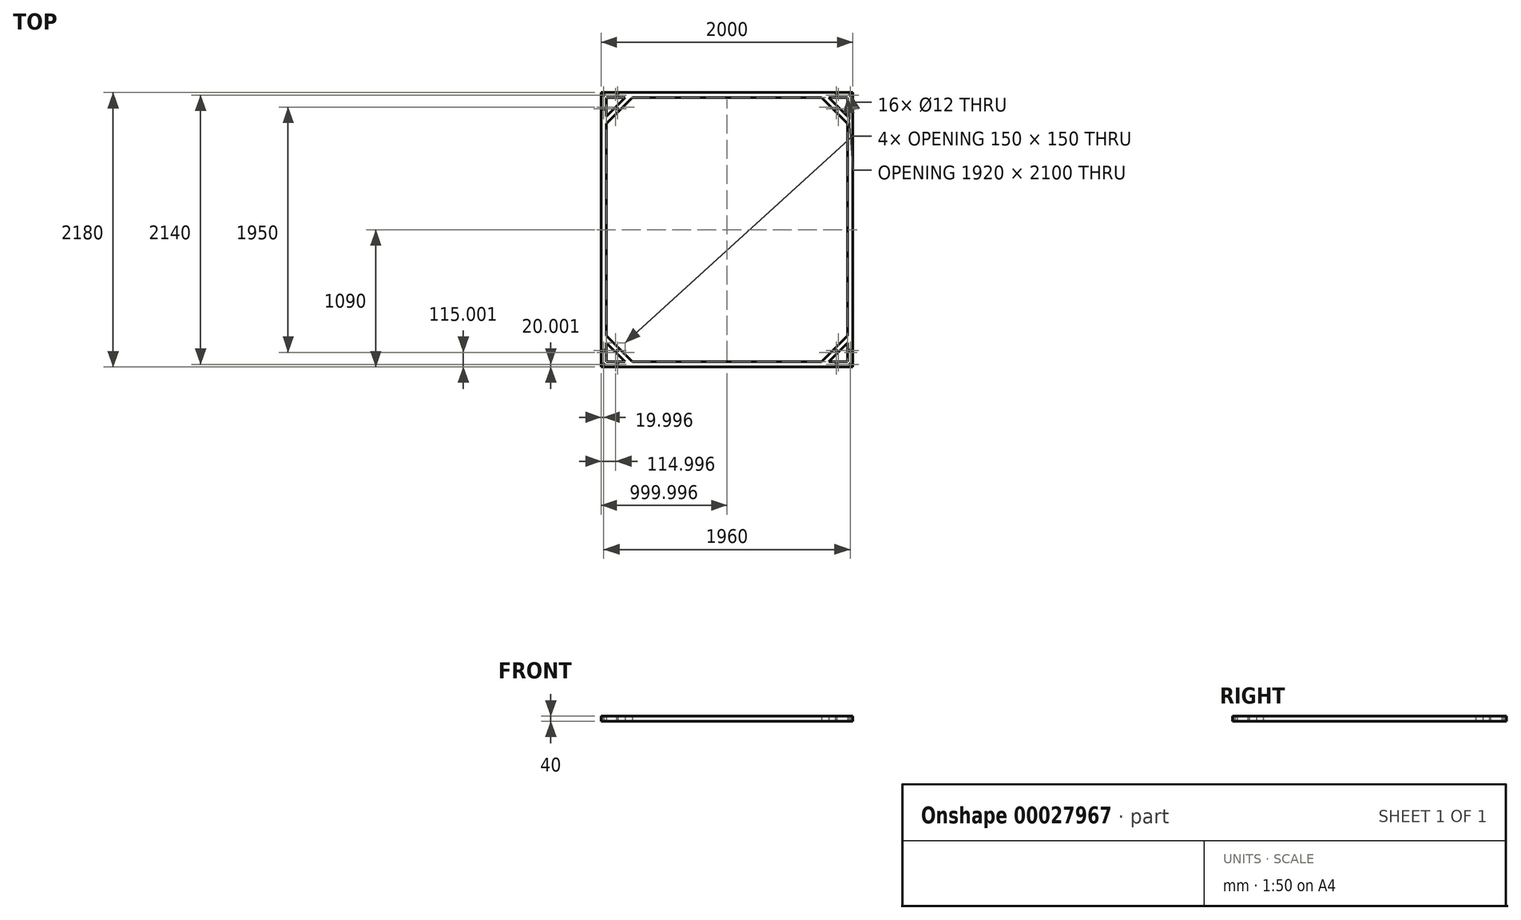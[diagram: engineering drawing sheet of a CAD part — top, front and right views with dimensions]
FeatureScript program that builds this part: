
annotation { "Feature Type Name" : "Feature", "Feature Type Description" : "" }
export const myFeature = defineFeature(function(context is Context, id is Id, definition is map)
    precondition{}
    {
        {
            var Q0;
            Q0=qCreatedBy(makeId("Top.planeOp"),FACE);
            var sketch = newSketch(context, id + "F0", { "sketchPlane" : qUnion([Q0])});
            skLineSegment(sketch, "E0.bottom", {"start": v(-446.06, 1599.63) * mm, "end": v(-406.06, 1599.63) * mm});
            skLineSegment(sketch, "E0.top", {"start": v(-446.06, -580.37) * mm, "end": v(-406.06, -580.37) * mm});
            skLineSegment(sketch, "E0.left", {"start": v(-446.06, 1599.63) * mm, "end": v(-446.06, -580.37) * mm});
            skLineSegment(sketch, "E0.right", {"start": v(-406.06, 1599.63) * mm, "end": v(-406.06, -580.37) * mm});
            skLineSegment(sketch, "E1.bottom", {"start": v(-406.06, 1599.63) * mm, "end": v(1513.94, 1599.63) * mm});
            skLineSegment(sketch, "E1.top", {"start": v(-406.06, 1559.63) * mm, "end": v(1513.94, 1559.63) * mm});
            skLineSegment(sketch, "E1.left", {"start": v(-406.06, 1599.63) * mm, "end": v(-406.06, 1559.63) * mm});
            skLineSegment(sketch, "E1.right", {"start": v(1513.94, 1599.63) * mm, "end": v(1513.94, 1559.63) * mm});
            skLineSegment(sketch, "E2.bottom", {"start": v(-406.06, -580.37) * mm, "end": v(1513.94, -580.37) * mm});
            skLineSegment(sketch, "E2.top", {"start": v(-406.06, -540.37) * mm, "end": v(1513.94, -540.37) * mm});
            skLineSegment(sketch, "E2.left", {"start": v(-406.06, -580.37) * mm, "end": v(-406.06, -540.37) * mm});
            skLineSegment(sketch, "E2.right", {"start": v(1513.94, -580.37) * mm, "end": v(1513.94, -540.37) * mm});
            skLineSegment(sketch, "E3", {"start": v(-406.06, 1409.63) * mm, "end": v(-256.06, 1559.63) * mm});
            skLineSegment(sketch, "E4", {"start": v(-256.06, 1559.63) * mm, "end": v(-199.5, 1559.63) * mm});
            skLineSegment(sketch, "E5", {"start": v(-199.5, 1559.63) * mm, "end": v(-406.06, 1353.06) * mm});
            skLineSegment(sketch, "E6", {"start": v(-406.06, 1353.06) * mm, "end": v(-406.06, 1409.63) * mm});
            skLineSegment(sketch, "E7.bottom", {"start": v(1513.94, 1599.63) * mm, "end": v(1553.94, 1599.63) * mm});
            skLineSegment(sketch, "E7.top", {"start": v(1513.94, -580.37) * mm, "end": v(1553.94, -580.37) * mm});
            skLineSegment(sketch, "E7.left", {"start": v(1513.94, 1599.63) * mm, "end": v(1513.94, -580.37) * mm});
            skLineSegment(sketch, "E7.right", {"start": v(1553.94, 1599.63) * mm, "end": v(1553.94, -580.37) * mm});
            skLineSegment(sketch, "E8", {"start": v(1513.94, 1409.63) * mm, "end": v(1363.94, 1559.63) * mm});
            skLineSegment(sketch, "E9", {"start": v(1363.94, 1559.63) * mm, "end": v(1307.37, 1559.63) * mm});
            skLineSegment(sketch, "E10", {"start": v(1307.37, 1559.63) * mm, "end": v(1513.94, 1353.06) * mm});
            skLineSegment(sketch, "E11", {"start": v(1513.94, 1353.06) * mm, "end": v(1513.94, 1409.63) * mm});
            skLineSegment(sketch, "E12", {"start": v(-256.06, -540.37) * mm, "end": v(-406.06, -390.37) * mm});
            skLineSegment(sketch, "E13", {"start": v(-406.06, -390.37) * mm, "end": v(-406.06, -333.8) * mm});
            skLineSegment(sketch, "E14", {"start": v(-406.06, -333.8) * mm, "end": v(-199.5, -540.37) * mm});
            skLineSegment(sketch, "E15", {"start": v(-199.5, -540.37) * mm, "end": v(-256.06, -540.37) * mm});
            skLineSegment(sketch, "E16", {"start": v(1363.94, -540.37) * mm, "end": v(1513.94, -390.37) * mm});
            skLineSegment(sketch, "E17", {"start": v(1513.94, -390.37) * mm, "end": v(1513.94, -333.8) * mm});
            skLineSegment(sketch, "E18", {"start": v(1513.94, -333.8) * mm, "end": v(1307.37, -540.37) * mm});
            skLineSegment(sketch, "E19", {"start": v(1307.37, -540.37) * mm, "end": v(1363.94, -540.37) * mm});
            skLineSegment(sketch, "E20", {"start": v(1307.37, 1559.63) * mm, "end": v(1363.94, 1559.63) * mm});
            skLineSegment(sketch, "E21", {"start": v(1513.94, 1409.63) * mm, "end": v(1513.94, 1353.06) * mm});
            skSolve(sketch);
        }
        {
            var Q0;
            Q0 = qSketchRegion(id + "F0", true);
            extrude(context, id + "F1", {"entities" : qUnion([Q0]), "depth" : 40 * mm});
        }
        {
            var Q0;
            Q0=makeQuery(id+"F0.imprint","IMPRINT",FACE,{"disambiguationData":[TD([[makeQuery(id+"F0.imprint","IMPRINT",EDGE,{"derivedFrom":sQuery(id+"F0.wireOp",EDGE,"E3")}),-1.0]])]});
            extrude(context, id + "F2", {"entities" : qUnion([Q0]), "operationType" : NewBodyOperationType.ADD, "depth" : 40 * mm});
        }
        {
            var Q0;
            Q0=makeQuery(id+"F0.imprint","IMPRINT",FACE,{"disambiguationData":[TD([[makeQuery(id+"F0.imprint","IMPRINT",EDGE,{"derivedFrom":sQuery(id+"F0.wireOp",EDGE,"E8")}),1.0]])]});
            extrude(context, id + "F3", {"entities" : qUnion([Q0]), "operationType" : NewBodyOperationType.ADD, "depth" : 40 * mm});
        }
        {
            var Q0;
            Q0=makeQuery(id+"F0.imprint","IMPRINT",FACE,{"disambiguationData":[TD([[makeQuery(id+"F0.imprint","IMPRINT",EDGE,{"derivedFrom":sQuery(id+"F0.wireOp",EDGE,"E12")}),-1.0]])]});
            extrude(context, id + "F4", {"entities" : qUnion([Q0]), "operationType" : NewBodyOperationType.ADD, "depth" : 40 * mm});
        }
        {
            var Q0;
            Q0=makeQuery(id+"F0.imprint","IMPRINT",FACE,{"disambiguationData":[TD([[makeQuery(id+"F0.imprint","IMPRINT",EDGE,{"derivedFrom":sQuery(id+"F0.wireOp",EDGE,"E16")}),1.0]])]});
            extrude(context, id + "F5", {"entities" : qUnion([Q0]), "operationType" : NewBodyOperationType.ADD, "depth" : 40 * mm});
        }
        {
            var Q0;
            {var subQ0=sQuery(id+"F0.wireOp",EDGE,"E4");var subQ1=sQuery(id+"F0.wireOp",EDGE,"E6");var subQ2=sQuery(id+"F0.wireOp",EDGE,"E13");var subQ3=sQuery(id+"F0.wireOp",EDGE,"E15");var subQ4=sQuery(id+"F0.wireOp",EDGE,"E17");var subQ5=sQuery(id+"F0.wireOp",EDGE,"E19");var subQ6=sQuery(id+"F0.wireOp",EDGE,"E20");var subQ7=sQuery(id+"F0.wireOp",EDGE,"E21");Q0=makeQuery(id+"F5.boolean.opBoolean","MERGE",FACE,{"derivedFrom":[makeQuery(id+"F4.boolean.opBoolean","MERGE",FACE,{"derivedFrom":[makeQuery(id+"F3.boolean.opBoolean","MERGE",FACE,{"derivedFrom":[makeQuery(id+"F2.boolean.opBoolean","MERGE",FACE,{"derivedFrom":[makeQuery(id+"F1.opExtrude","CAP_FACE",FACE,{"disambiguationData":[OSD([sQuery(id+"F0.wireOp",EDGE,"E0.bottom"),sQuery(id+"F0.wireOp",EDGE,"E0.top"),sQuery(id+"F0.wireOp",EDGE,"E0.left"),sQuery(id+"F0.wireOp",EDGE,"E0.right"),sQuery(id+"F0.wireOp",EDGE,"E1.bottom"),sQuery(id+"F0.wireOp",EDGE,"E1.top"),sQuery(id+"F0.wireOp",EDGE,"E2.bottom"),sQuery(id+"F0.wireOp",EDGE,"E2.top"),subQ0,subQ1,sQuery(id+"F0.wireOp",EDGE,"E7.bottom"),sQuery(id+"F0.wireOp",EDGE,"E7.top"),sQuery(id+"F0.wireOp",EDGE,"E7.left"),sQuery(id+"F0.wireOp",EDGE,"E7.right"),subQ2,subQ3,subQ4,subQ5,subQ6,subQ7])],"isStart":false}),makeQuery(id+"F2.opExtrude","CAP_FACE",FACE,{"disambiguationData":[OSD([sQuery(id+"F0.wireOp",EDGE,"E3"),subQ0,sQuery(id+"F0.wireOp",EDGE,"E5"),subQ1])],"isStart":false})]}),makeQuery(id+"F3.opExtrude","CAP_FACE",FACE,{"disambiguationData":[OSD([sQuery(id+"F0.wireOp",EDGE,"E8"),sQuery(id+"F0.wireOp",EDGE,"E10"),subQ6,subQ7])],"isStart":false})]}),makeQuery(id+"F4.opExtrude","CAP_FACE",FACE,{"disambiguationData":[OSD([sQuery(id+"F0.wireOp",EDGE,"E12"),subQ2,sQuery(id+"F0.wireOp",EDGE,"E14"),subQ3])],"isStart":false})]}),makeQuery(id+"F5.opExtrude","CAP_FACE",FACE,{"disambiguationData":[OSD([sQuery(id+"F0.wireOp",EDGE,"E16"),subQ4,sQuery(id+"F0.wireOp",EDGE,"E18"),subQ5])],"isStart":false})]});}
            var sketch = newSketch(context, id + "F6", { "sketchPlane" : qUnion([Q0])});
            skCircle(sketch, "E22", {"center": v(-316.06, 1469.63) * mm, "radius": 6 * mm});
            skCircle(sketch, "E23", {"center": v(-426.06, 1469.63) * mm, "radius": 6 * mm});
            skCircle(sketch, "E24", {"center": v(-426.06, 1579.63) * mm, "radius": 6 * mm});
            skCircle(sketch, "E25", {"center": v(-316.06, 1579.63) * mm, "radius": 6 * mm});
            skSolve(sketch);
        }
        {
            var Q0;
            Q0=sQuery(id+"F6.wireOp",VERTEX,"E24.center");
            var Q1;
            Q1=sQuery(id+"F6.wireOp",VERTEX,"E25.center");
            var Q2;
            Q2=sQuery(id+"F6.wireOp",VERTEX,"E22.center");
            var Q3;
            Q3=sQuery(id+"F6.wireOp",VERTEX,"E23.center");
            var Q4;
            Q4=makeQuery(id+"F1.opExtrude","SWEPT_BODY",BODY,{"disambiguationData":[OSD([sQuery(id+"F0.wireOp",EDGE,"E0.bottom"),sQuery(id+"F0.wireOp",EDGE,"E0.top"),sQuery(id+"F0.wireOp",EDGE,"E0.left"),sQuery(id+"F0.wireOp",EDGE,"E0.right"),sQuery(id+"F0.wireOp",EDGE,"E1.bottom"),sQuery(id+"F0.wireOp",EDGE,"E1.top"),sQuery(id+"F0.wireOp",EDGE,"E2.bottom"),sQuery(id+"F0.wireOp",EDGE,"E2.top"),sQuery(id+"F0.wireOp",EDGE,"E4"),sQuery(id+"F0.wireOp",EDGE,"E6"),sQuery(id+"F0.wireOp",EDGE,"E7.bottom"),sQuery(id+"F0.wireOp",EDGE,"E7.top"),sQuery(id+"F0.wireOp",EDGE,"E7.left"),sQuery(id+"F0.wireOp",EDGE,"E7.right"),sQuery(id+"F0.wireOp",EDGE,"E13"),sQuery(id+"F0.wireOp",EDGE,"E15"),sQuery(id+"F0.wireOp",EDGE,"E17"),sQuery(id+"F0.wireOp",EDGE,"E19"),sQuery(id+"F0.wireOp",EDGE,"E20"),sQuery(id+"F0.wireOp",EDGE,"E21")])]});
            hole(context, id + "F7", {"style" : HoleStyle.SIMPLE, "holeDiameter" : 12 * mm, "endStyle" : HoleEndStyle.BLIND, "holeDepth" : 40 * mm, "locations" : qUnion([Q0, Q1, Q2, Q3]), "scope" : qUnion([Q4])});
        }
        {
            var Q0;
            {var subQ0=sQuery(id+"F0.wireOp",EDGE,"E4");var subQ1=sQuery(id+"F0.wireOp",EDGE,"E6");var subQ2=sQuery(id+"F0.wireOp",EDGE,"E13");var subQ3=sQuery(id+"F0.wireOp",EDGE,"E15");var subQ4=sQuery(id+"F0.wireOp",EDGE,"E17");var subQ5=sQuery(id+"F0.wireOp",EDGE,"E19");var subQ6=sQuery(id+"F0.wireOp",EDGE,"E20");var subQ7=sQuery(id+"F0.wireOp",EDGE,"E21");Q0=makeQuery(id+"F5.boolean.opBoolean","MERGE",FACE,{"derivedFrom":[makeQuery(id+"F4.boolean.opBoolean","MERGE",FACE,{"derivedFrom":[makeQuery(id+"F3.boolean.opBoolean","MERGE",FACE,{"derivedFrom":[makeQuery(id+"F2.boolean.opBoolean","MERGE",FACE,{"derivedFrom":[makeQuery(id+"F1.opExtrude","CAP_FACE",FACE,{"disambiguationData":[OSD([sQuery(id+"F0.wireOp",EDGE,"E0.bottom"),sQuery(id+"F0.wireOp",EDGE,"E0.top"),sQuery(id+"F0.wireOp",EDGE,"E0.left"),sQuery(id+"F0.wireOp",EDGE,"E0.right"),sQuery(id+"F0.wireOp",EDGE,"E1.bottom"),sQuery(id+"F0.wireOp",EDGE,"E1.top"),sQuery(id+"F0.wireOp",EDGE,"E2.bottom"),sQuery(id+"F0.wireOp",EDGE,"E2.top"),subQ0,subQ1,sQuery(id+"F0.wireOp",EDGE,"E7.bottom"),sQuery(id+"F0.wireOp",EDGE,"E7.top"),sQuery(id+"F0.wireOp",EDGE,"E7.left"),sQuery(id+"F0.wireOp",EDGE,"E7.right"),subQ2,subQ3,subQ4,subQ5,subQ6,subQ7])],"isStart":false}),makeQuery(id+"F2.opExtrude","CAP_FACE",FACE,{"disambiguationData":[OSD([sQuery(id+"F0.wireOp",EDGE,"E3"),subQ0,sQuery(id+"F0.wireOp",EDGE,"E5"),subQ1])],"isStart":false})]}),makeQuery(id+"F3.opExtrude","CAP_FACE",FACE,{"disambiguationData":[OSD([sQuery(id+"F0.wireOp",EDGE,"E8"),sQuery(id+"F0.wireOp",EDGE,"E10"),subQ6,subQ7])],"isStart":false})]}),makeQuery(id+"F4.opExtrude","CAP_FACE",FACE,{"disambiguationData":[OSD([sQuery(id+"F0.wireOp",EDGE,"E12"),subQ2,sQuery(id+"F0.wireOp",EDGE,"E14"),subQ3])],"isStart":false})]}),makeQuery(id+"F5.opExtrude","CAP_FACE",FACE,{"disambiguationData":[OSD([sQuery(id+"F0.wireOp",EDGE,"E16"),subQ4,sQuery(id+"F0.wireOp",EDGE,"E18"),subQ5])],"isStart":false})]});}
            var sketch = newSketch(context, id + "F8", { "sketchPlane" : qUnion([Q0])});
            skCircle(sketch, "E26", {"center": v(1423.94, 1579.63) * mm, "radius": 6 * mm});
            skCircle(sketch, "E27", {"center": v(1533.94, 1579.63) * mm, "radius": 6 * mm});
            skCircle(sketch, "E28", {"center": v(1423.94, 1469.63) * mm, "radius": 6 * mm});
            skCircle(sketch, "E29", {"center": v(1533.94, 1469.63) * mm, "radius": 6 * mm});
            skSolve(sketch);
        }
        {
            var Q0;
            Q0=sQuery(id+"F8.wireOp",VERTEX,"E26.center");
            var Q1;
            Q1=sQuery(id+"F8.wireOp",VERTEX,"E27.center");
            var Q2;
            Q2=sQuery(id+"F8.wireOp",VERTEX,"E28.center");
            var Q3;
            Q3=sQuery(id+"F8.wireOp",VERTEX,"E29.center");
            var Q4;
            Q4=makeQuery(id+"F1.opExtrude","SWEPT_BODY",BODY,{"disambiguationData":[OSD([sQuery(id+"F0.wireOp",EDGE,"E0.bottom"),sQuery(id+"F0.wireOp",EDGE,"E0.top"),sQuery(id+"F0.wireOp",EDGE,"E0.left"),sQuery(id+"F0.wireOp",EDGE,"E0.right"),sQuery(id+"F0.wireOp",EDGE,"E1.bottom"),sQuery(id+"F0.wireOp",EDGE,"E1.top"),sQuery(id+"F0.wireOp",EDGE,"E2.bottom"),sQuery(id+"F0.wireOp",EDGE,"E2.top"),sQuery(id+"F0.wireOp",EDGE,"E4"),sQuery(id+"F0.wireOp",EDGE,"E6"),sQuery(id+"F0.wireOp",EDGE,"E7.bottom"),sQuery(id+"F0.wireOp",EDGE,"E7.top"),sQuery(id+"F0.wireOp",EDGE,"E7.left"),sQuery(id+"F0.wireOp",EDGE,"E7.right"),sQuery(id+"F0.wireOp",EDGE,"E13"),sQuery(id+"F0.wireOp",EDGE,"E15"),sQuery(id+"F0.wireOp",EDGE,"E17"),sQuery(id+"F0.wireOp",EDGE,"E19"),sQuery(id+"F0.wireOp",EDGE,"E20"),sQuery(id+"F0.wireOp",EDGE,"E21")])]});
            hole(context, id + "F9", {"style" : HoleStyle.SIMPLE, "holeDiameter" : 12 * mm, "endStyle" : HoleEndStyle.THROUGH, "locations" : qUnion([Q0, Q1, Q2, Q3]), "scope" : qUnion([Q4])});
        }
        {
            var Q0;
            {var subQ0=sQuery(id+"F0.wireOp",EDGE,"E4");var subQ1=sQuery(id+"F0.wireOp",EDGE,"E6");var subQ2=sQuery(id+"F0.wireOp",EDGE,"E13");var subQ3=sQuery(id+"F0.wireOp",EDGE,"E15");var subQ4=sQuery(id+"F0.wireOp",EDGE,"E17");var subQ5=sQuery(id+"F0.wireOp",EDGE,"E19");var subQ6=sQuery(id+"F0.wireOp",EDGE,"E20");var subQ7=sQuery(id+"F0.wireOp",EDGE,"E21");Q0=makeQuery(id+"F5.boolean.opBoolean","MERGE",FACE,{"derivedFrom":[makeQuery(id+"F4.boolean.opBoolean","MERGE",FACE,{"derivedFrom":[makeQuery(id+"F3.boolean.opBoolean","MERGE",FACE,{"derivedFrom":[makeQuery(id+"F2.boolean.opBoolean","MERGE",FACE,{"derivedFrom":[makeQuery(id+"F1.opExtrude","CAP_FACE",FACE,{"disambiguationData":[OSD([sQuery(id+"F0.wireOp",EDGE,"E0.bottom"),sQuery(id+"F0.wireOp",EDGE,"E0.top"),sQuery(id+"F0.wireOp",EDGE,"E0.left"),sQuery(id+"F0.wireOp",EDGE,"E0.right"),sQuery(id+"F0.wireOp",EDGE,"E1.bottom"),sQuery(id+"F0.wireOp",EDGE,"E1.top"),sQuery(id+"F0.wireOp",EDGE,"E2.bottom"),sQuery(id+"F0.wireOp",EDGE,"E2.top"),subQ0,subQ1,sQuery(id+"F0.wireOp",EDGE,"E7.bottom"),sQuery(id+"F0.wireOp",EDGE,"E7.top"),sQuery(id+"F0.wireOp",EDGE,"E7.left"),sQuery(id+"F0.wireOp",EDGE,"E7.right"),subQ2,subQ3,subQ4,subQ5,subQ6,subQ7])],"isStart":false}),makeQuery(id+"F2.opExtrude","CAP_FACE",FACE,{"disambiguationData":[OSD([sQuery(id+"F0.wireOp",EDGE,"E3"),subQ0,sQuery(id+"F0.wireOp",EDGE,"E5"),subQ1])],"isStart":false})]}),makeQuery(id+"F3.opExtrude","CAP_FACE",FACE,{"disambiguationData":[OSD([sQuery(id+"F0.wireOp",EDGE,"E8"),sQuery(id+"F0.wireOp",EDGE,"E10"),subQ6,subQ7])],"isStart":false})]}),makeQuery(id+"F4.opExtrude","CAP_FACE",FACE,{"disambiguationData":[OSD([sQuery(id+"F0.wireOp",EDGE,"E12"),subQ2,sQuery(id+"F0.wireOp",EDGE,"E14"),subQ3])],"isStart":false})]}),makeQuery(id+"F5.opExtrude","CAP_FACE",FACE,{"disambiguationData":[OSD([sQuery(id+"F0.wireOp",EDGE,"E16"),subQ4,sQuery(id+"F0.wireOp",EDGE,"E18"),subQ5])],"isStart":false})]});}
            var sketch = newSketch(context, id + "F10", { "sketchPlane" : qUnion([Q0])});
            skCircle(sketch, "E30", {"center": v(-426.06, -560.37) * mm, "radius": 6 * mm});
            skCircle(sketch, "E31", {"center": v(-316.06, -560.37) * mm, "radius": 6 * mm});
            skCircle(sketch, "E32", {"center": v(-316.06, -450.37) * mm, "radius": 6 * mm});
            skCircle(sketch, "E33", {"center": v(-426.06, -450.37) * mm, "radius": 6 * mm});
            skSolve(sketch);
        }
        {
            var Q0;
            Q0=sQuery(id+"F10.wireOp",VERTEX,"E33.center");
            var Q1;
            Q1=sQuery(id+"F10.wireOp",VERTEX,"E32.center");
            var Q2;
            Q2=sQuery(id+"F10.wireOp",VERTEX,"E31.center");
            var Q3;
            Q3=sQuery(id+"F10.wireOp",VERTEX,"E30.center");
            var Q4;
            Q4=makeQuery(id+"F1.opExtrude","SWEPT_BODY",BODY,{"disambiguationData":[OSD([sQuery(id+"F0.wireOp",EDGE,"E0.bottom"),sQuery(id+"F0.wireOp",EDGE,"E0.top"),sQuery(id+"F0.wireOp",EDGE,"E0.left"),sQuery(id+"F0.wireOp",EDGE,"E0.right"),sQuery(id+"F0.wireOp",EDGE,"E1.bottom"),sQuery(id+"F0.wireOp",EDGE,"E1.top"),sQuery(id+"F0.wireOp",EDGE,"E2.bottom"),sQuery(id+"F0.wireOp",EDGE,"E2.top"),sQuery(id+"F0.wireOp",EDGE,"E4"),sQuery(id+"F0.wireOp",EDGE,"E6"),sQuery(id+"F0.wireOp",EDGE,"E7.bottom"),sQuery(id+"F0.wireOp",EDGE,"E7.top"),sQuery(id+"F0.wireOp",EDGE,"E7.left"),sQuery(id+"F0.wireOp",EDGE,"E7.right"),sQuery(id+"F0.wireOp",EDGE,"E13"),sQuery(id+"F0.wireOp",EDGE,"E15"),sQuery(id+"F0.wireOp",EDGE,"E17"),sQuery(id+"F0.wireOp",EDGE,"E19"),sQuery(id+"F0.wireOp",EDGE,"E20"),sQuery(id+"F0.wireOp",EDGE,"E21")])]});
            hole(context, id + "F11", {"style" : HoleStyle.SIMPLE, "holeDiameter" : 12 * mm, "endStyle" : HoleEndStyle.THROUGH, "locations" : qUnion([Q0, Q1, Q2, Q3]), "scope" : qUnion([Q4])});
        }
        {
            var Q0;
            {var subQ0=sQuery(id+"F0.wireOp",EDGE,"E4");var subQ1=sQuery(id+"F0.wireOp",EDGE,"E6");var subQ2=sQuery(id+"F0.wireOp",EDGE,"E13");var subQ3=sQuery(id+"F0.wireOp",EDGE,"E15");var subQ4=sQuery(id+"F0.wireOp",EDGE,"E17");var subQ5=sQuery(id+"F0.wireOp",EDGE,"E19");var subQ6=sQuery(id+"F0.wireOp",EDGE,"E20");var subQ7=sQuery(id+"F0.wireOp",EDGE,"E21");Q0=makeQuery(id+"F5.boolean.opBoolean","MERGE",FACE,{"derivedFrom":[makeQuery(id+"F4.boolean.opBoolean","MERGE",FACE,{"derivedFrom":[makeQuery(id+"F3.boolean.opBoolean","MERGE",FACE,{"derivedFrom":[makeQuery(id+"F2.boolean.opBoolean","MERGE",FACE,{"derivedFrom":[makeQuery(id+"F1.opExtrude","CAP_FACE",FACE,{"disambiguationData":[OSD([sQuery(id+"F0.wireOp",EDGE,"E0.bottom"),sQuery(id+"F0.wireOp",EDGE,"E0.top"),sQuery(id+"F0.wireOp",EDGE,"E0.left"),sQuery(id+"F0.wireOp",EDGE,"E0.right"),sQuery(id+"F0.wireOp",EDGE,"E1.bottom"),sQuery(id+"F0.wireOp",EDGE,"E1.top"),sQuery(id+"F0.wireOp",EDGE,"E2.bottom"),sQuery(id+"F0.wireOp",EDGE,"E2.top"),subQ0,subQ1,sQuery(id+"F0.wireOp",EDGE,"E7.bottom"),sQuery(id+"F0.wireOp",EDGE,"E7.top"),sQuery(id+"F0.wireOp",EDGE,"E7.left"),sQuery(id+"F0.wireOp",EDGE,"E7.right"),subQ2,subQ3,subQ4,subQ5,subQ6,subQ7])],"isStart":false}),makeQuery(id+"F2.opExtrude","CAP_FACE",FACE,{"disambiguationData":[OSD([sQuery(id+"F0.wireOp",EDGE,"E3"),subQ0,sQuery(id+"F0.wireOp",EDGE,"E5"),subQ1])],"isStart":false})]}),makeQuery(id+"F3.opExtrude","CAP_FACE",FACE,{"disambiguationData":[OSD([sQuery(id+"F0.wireOp",EDGE,"E8"),sQuery(id+"F0.wireOp",EDGE,"E10"),subQ6,subQ7])],"isStart":false})]}),makeQuery(id+"F4.opExtrude","CAP_FACE",FACE,{"disambiguationData":[OSD([sQuery(id+"F0.wireOp",EDGE,"E12"),subQ2,sQuery(id+"F0.wireOp",EDGE,"E14"),subQ3])],"isStart":false})]}),makeQuery(id+"F5.opExtrude","CAP_FACE",FACE,{"disambiguationData":[OSD([sQuery(id+"F0.wireOp",EDGE,"E16"),subQ4,sQuery(id+"F0.wireOp",EDGE,"E18"),subQ5])],"isStart":false})]});}
            var sketch = newSketch(context, id + "F12", { "sketchPlane" : qUnion([Q0])});
            skCircle(sketch, "E34", {"center": v(1533.94, -560.37) * mm, "radius": 6 * mm});
            skCircle(sketch, "E35", {"center": v(1423.94, -560.37) * mm, "radius": 6 * mm});
            skCircle(sketch, "E36", {"center": v(1423.94, -450.37) * mm, "radius": 6 * mm});
            skCircle(sketch, "E37", {"center": v(1533.94, -450.37) * mm, "radius": 6 * mm});
            skSolve(sketch);
        }
        {
            var Q0;
            Q0=sQuery(id+"F12.wireOp",VERTEX,"E36.center");
            var Q1;
            Q1=sQuery(id+"F12.wireOp",VERTEX,"E37.center");
            var Q2;
            Q2=sQuery(id+"F12.wireOp",VERTEX,"E35.center");
            var Q3;
            Q3=sQuery(id+"F12.wireOp",VERTEX,"E34.center");
            var Q4;
            Q4=makeQuery(id+"F1.opExtrude","SWEPT_BODY",BODY,{"disambiguationData":[OSD([sQuery(id+"F0.wireOp",EDGE,"E0.bottom"),sQuery(id+"F0.wireOp",EDGE,"E0.top"),sQuery(id+"F0.wireOp",EDGE,"E0.left"),sQuery(id+"F0.wireOp",EDGE,"E0.right"),sQuery(id+"F0.wireOp",EDGE,"E1.bottom"),sQuery(id+"F0.wireOp",EDGE,"E1.top"),sQuery(id+"F0.wireOp",EDGE,"E2.bottom"),sQuery(id+"F0.wireOp",EDGE,"E2.top"),sQuery(id+"F0.wireOp",EDGE,"E4"),sQuery(id+"F0.wireOp",EDGE,"E6"),sQuery(id+"F0.wireOp",EDGE,"E7.bottom"),sQuery(id+"F0.wireOp",EDGE,"E7.top"),sQuery(id+"F0.wireOp",EDGE,"E7.left"),sQuery(id+"F0.wireOp",EDGE,"E7.right"),sQuery(id+"F0.wireOp",EDGE,"E13"),sQuery(id+"F0.wireOp",EDGE,"E15"),sQuery(id+"F0.wireOp",EDGE,"E17"),sQuery(id+"F0.wireOp",EDGE,"E19"),sQuery(id+"F0.wireOp",EDGE,"E20"),sQuery(id+"F0.wireOp",EDGE,"E21")])]});
            hole(context, id + "F13", {"style" : HoleStyle.SIMPLE, "holeDiameter" : 12 * mm, "endStyle" : HoleEndStyle.THROUGH, "locations" : qUnion([Q0, Q1, Q2, Q3]), "scope" : qUnion([Q4])});
        }
    });
